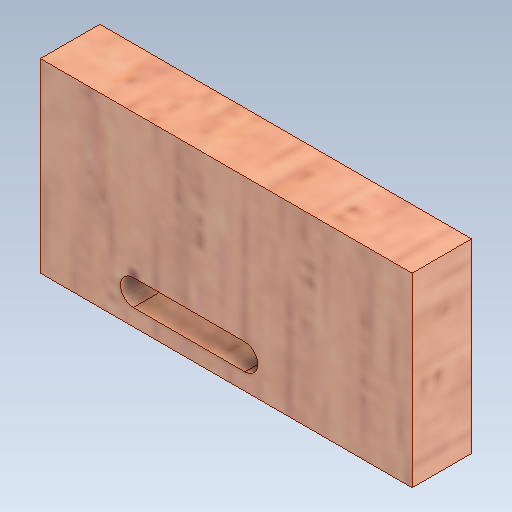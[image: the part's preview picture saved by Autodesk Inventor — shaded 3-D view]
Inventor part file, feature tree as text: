
AUTODESK INVENTOR PART (.ipt)
format: ipt  version: 2020 (Build 240168000, 168)  size: 246,272 bytes
history: native  units: mm
features: extrude x2, sketch x2
ambient origin geometry x8: Origin, YZ Plane, XZ Plane, XY Plane, X Axis, Y Axis, Z Axis, Center Point
bodies: Solid1 (feature_tree)
feature tree (4):
  extrude  "Extrusion1"  Depth=25.0mm
  extrude  "Extrusion5"  Depth=3.5mm
  sketch  "Sketch1"  dims[d0=50.0mm d1=25.0mm]
  sketch  "Sketch5"  dims[d2=8.0mm d3=0.0mm d29=3.5mm d30=4.0mm d31=4.0mm d32=20.0mm d33=15.0mm d34=15.0mm d35=0.0mm]
